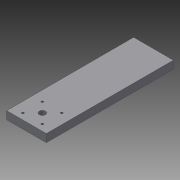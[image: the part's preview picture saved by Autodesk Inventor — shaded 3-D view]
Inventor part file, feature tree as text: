
AUTODESK INVENTOR PART (.ipt)
format: ipt  version: 2015 (Build 190159000, 159)  size: 89,600 bytes
history: native  units: in
note: dims shown in document units (in); Inventor stores cm internally (conversion verified against a paired STEP export)
features: sketch x3, hole x2, extrude x1
ambient origin geometry x8: Origin, YZ Plane, XZ Plane, XY Plane, X Axis, Y Axis, Z Axis, Center Point
bodies: Solid1 (feature_tree)
feature tree (6):
  extrude  "Extrusion1"  Depth=8.0in
  hole  "Hole1"  [1 undecoded]
  hole  "Hole2"  [1 undecoded]
  sketch  "Sketch1"  dims[d0=2.5in d1=8.0in]
  sketch  "Sketch2"  dims[d2=0.5in d3=0.0in d6=3.0in]
  sketch  "Sketch4"  dims[d7=1.2205in d8=1.22in d9=0.1378in d10=0.75in d11=0.375in d12=0.25in d13=0.5635in d14=1.0in d15=0.8108in d16=0.3937in d17=0.75in d18=0.375in d19=0.25in d20=0.5635in d21=1.0in d22=0.8108in]
note: 2 required parameter values undecoded (feature->parameter linkage not recoverable at this tier; creation-order binding heuristic only, values carry confidence <= 0.55)
